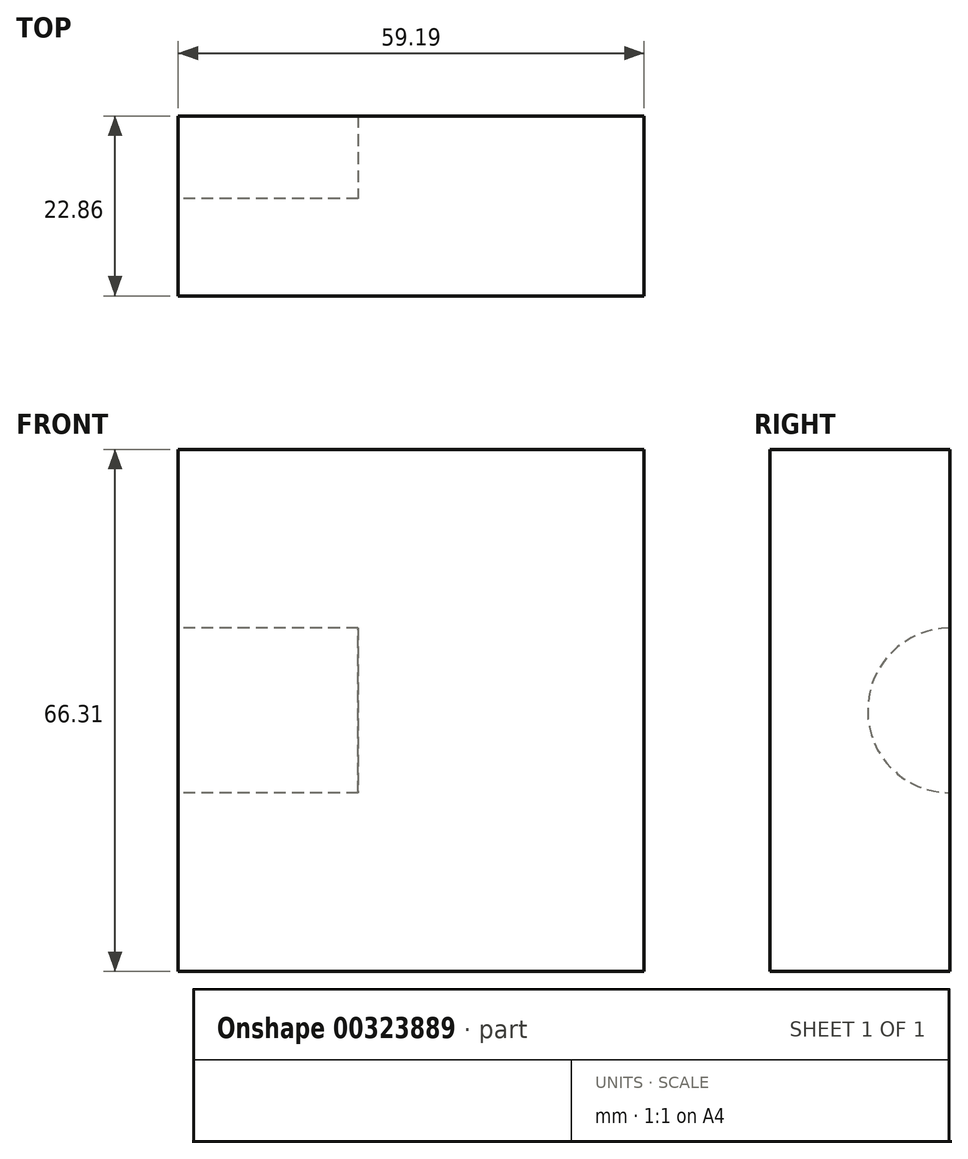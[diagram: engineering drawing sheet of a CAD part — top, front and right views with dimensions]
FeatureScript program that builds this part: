
annotation { "Feature Type Name" : "Feature", "Feature Type Description" : "" }
export const myFeature = defineFeature(function(context is Context, id is Id, definition is map)
    precondition{}
    {
        {
            var Q0;
            Q0=qCreatedBy(makeId("Front.planeOp"),FACE);
            var sketch = newSketch(context, id + "F0", { "sketchPlane" : qUnion([Q0])});
            skLineSegment(sketch, "E0.bottom", {"start": v(-133.97, 16.74) * mm, "end": v(-74.78, 16.74) * mm});
            skLineSegment(sketch, "E0.top", {"start": v(-133.97, -49.57) * mm, "end": v(-74.78, -49.57) * mm});
            skLineSegment(sketch, "E0.left", {"start": v(-133.97, 16.74) * mm, "end": v(-133.97, -49.57) * mm});
            skLineSegment(sketch, "E0.right", {"start": v(-74.78, 16.74) * mm, "end": v(-74.78, -49.57) * mm});
            skSolve(sketch);
        }
        {
            var Q0;
            Q0=qSketchRegion(id+"F0",true);
            extrude(context, id + "F1", {"entities" : qUnion([Q0]), "depth" : 22.86 * mm});
        }
        {
            var Q0;
            Q0=makeQuery(id+"F1.opExtrude","SWEPT_FACE",FACE,{"disambiguationData":[OSD([sQuery(id+"F0.wireOp",EDGE,"E0.left")])]});
            var sketch = newSketch(context, id + "F2", { "sketchPlane" : qUnion([Q0])});
            skCircle(sketch, "E1", {"center": v(0, -16.41) * mm, "radius": 10.46 * mm});
            skSolve(sketch);
        }
        {
            var Q0;
            Q0=qSketchRegion(id+"F2",true);
            extrude(context, id + "F3", {"entities" : qUnion([Q0]), "operationType" : NewBodyOperationType.REMOVE, "oppositeDirection" : true, "depth" : 22.86 * mm});
        }
    });
